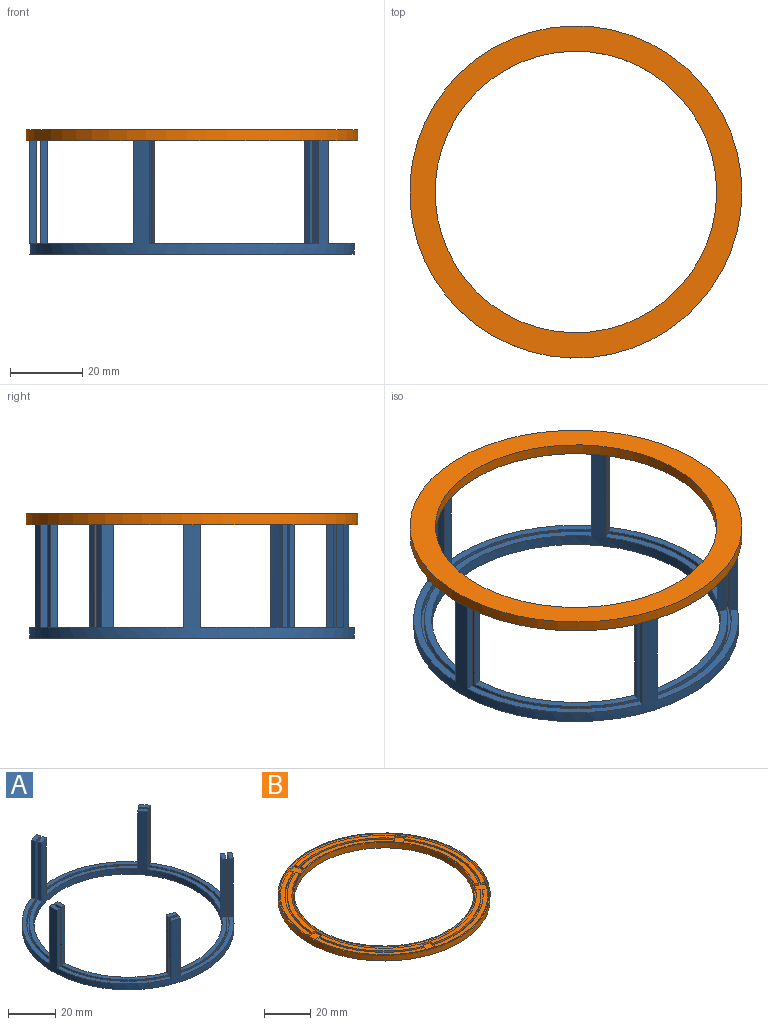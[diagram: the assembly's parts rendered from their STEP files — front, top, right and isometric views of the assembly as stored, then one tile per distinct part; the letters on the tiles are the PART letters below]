
ASSEMBLY  parts=2 mates=1
PART A: 46 faces, bbox 90x90x33 mm
  f0: plane 37.12x27.61mm, normal (0,0,1), area 94.5mm2, adj f10,f14,f16,f44
  f1: plane 39.76x29.53mm, normal (0,0,1), area 101.4mm2, adj f11,f15,f19,f41
  f2: plane 43.51x16.83mm, normal (0,0,1), area 94.5mm2, adj f10,f14,f38,f43
  f3: plane 46.62x17.94mm, normal (0,0,1), area 101.4mm2, adj f11,f15,f35,f40
  f4: plane 49.02x8.94mm, normal (0,0,1), area 101.4mm2, adj f11,f15,f32,f34
  f5: plane 45.75x8.45mm, normal (0,0,1), area 94.5mm2, adj f10,f14,f29,f37
  f6: plane 46.62x17.94mm, normal (0,0,1), area 101.4mm2, adj f11,f15,f26,f31
  f7: plane 43.51x16.83mm, normal (0,0,1), area 94.5mm2, adj f10,f14,f23,f28
  f8: plane 39.76x29.53mm, normal (0,0,1), area 101.4mm2, adj f11,f15,f20,f25
  f9: plane 37.12x27.61mm, normal (0,0,1), area 94.5mm2, adj f10,f14,f17,f22
  f10: cylinder r=40mm len=80mm, axis (0,0,-1), area 1382.3mm2, adj f0,f2,f5,f7,f9,f13,f16,f17
  f11: cylinder r=45mm len=90mm, axis (0,0,-1), area 1555.1mm2, adj f1,f3,f4,f6,f8,f13,f19,f20
  f12: plane 86x86mm, normal (0,0,1), area 267mm2, adj f14,f15
  f13: plane 90x90mm, normal (0,0,-1), area 1335.2mm2, adj f10,f11
  f14: cylinder r=42mm len=84mm, axis (0,0,-1), area 1187.5mm2, adj f0,f2,f5,f7,f9,f12,f16,f17
  f15: cylinder r=43mm len=86mm, axis (0,0,-1), area 1215.8mm2, adj f1,f3,f4,f6,f8,f12,f19,f20
  f16: plane 30x2mm, normal (0.05,1,0), area 60mm2, adj f0,f10,f14,f18
  f17: plane 30x2mm, normal (0.05,-1,0), area 60mm2, adj f9,f10,f14,f18
  f18: plane 4.4x2.06mm, normal (0,0,1), area 8.6mm2, adj f10,f14,f16,f17
  f19: plane 30x2mm, normal (0.05,1,0), area 60mm2, adj f1,f11,f15,f21
  f20: plane 30x2mm, normal (0.05,-1,0), area 60mm2, adj f8,f11,f15,f21
  f21: plane 4.71x2.06mm, normal (0,0,1), area 9.2mm2, adj f11,f15,f19,f20
  f22: plane 30x1.87mm, normal (-0.93,0.36,0), area 60mm2, adj f9,f10,f14,f24
  f23: plane 30x1.93mm, normal (0.97,-0.26,0), area 60mm2, adj f7,f10,f14,f24
  f24: plane 4.7x3.23mm, normal (0,0,1), area 8.6mm2, adj f10,f14,f22,f23
  f25: plane 30x1.87mm, normal (-0.93,0.36,0), area 60mm2, adj f8,f11,f15,f27
  f26: plane 30x1.93mm, normal (0.97,-0.26,0), area 60mm2, adj f6,f11,f15,f27
  f27: plane 5x3.32mm, normal (0,0,1), area 9.2mm2, adj f11,f15,f25,f26
  f28: plane 30x1.55mm, normal (-0.63,-0.78,0), area 60mm2, adj f7,f10,f14,f30
  f29: plane 30x1.68mm, normal (0.54,0.84,0), area 60mm2, adj f5,f10,f14,f30
  f30: plane 4.65x4.14mm, normal (0,0,1), area 8.6mm2, adj f10,f14,f28,f29
  f31: plane 30x1.55mm, normal (-0.63,-0.78,0), area 60mm2, adj f6,f11,f15,f33
  f32: plane 30x1.68mm, normal (0.54,0.84,0), area 60mm2, adj f4,f11,f15,f33
  f33: plane 4.9x4.32mm, normal (0,0,1), area 9.2mm2, adj f11,f15,f31,f32
  f34: plane 30x1.68mm, normal (0.54,-0.84,0), area 60mm2, adj f4,f11,f15,f36
  f35: plane 30x1.55mm, normal (-0.63,0.78,0), area 60mm2, adj f3,f11,f15,f36
  f36: plane 4.9x4.32mm, normal (0,0,1), area 9.2mm2, adj f11,f15,f34,f35
  f37: plane 30x1.68mm, normal (0.54,-0.84,0), area 60mm2, adj f5,f10,f14,f39
  f38: plane 30x1.55mm, normal (-0.63,0.78,0), area 60mm2, adj f2,f10,f14,f39
  f39: plane 4.65x4.14mm, normal (0,0,1), area 8.6mm2, adj f10,f14,f37,f38
  f40: plane 30x1.93mm, normal (0.97,0.26,0), area 60mm2, adj f3,f11,f15,f42
  f41: plane 30x1.87mm, normal (-0.93,-0.36,0), area 60mm2, adj f1,f11,f15,f42
  f42: plane 5x3.32mm, normal (0,0,1), area 9.2mm2, adj f11,f15,f40,f41
  f43: plane 30x1.93mm, normal (0.97,0.26,0), area 60mm2, adj f2,f10,f14,f45
  f44: plane 30x1.87mm, normal (-0.93,-0.36,0), area 60mm2, adj f0,f10,f14,f45
  f45: plane 4.7x3.23mm, normal (0,0,1), area 8.6mm2, adj f10,f14,f43,f44
PART B: 58 faces, bbox 92x92x3 mm
  f0: plane 43.39x16.77mm, normal (0,0,1), area 94.2mm2, adj f10,f25,f50,f55
  f1: plane 45.63x8.42mm, normal (0,0,1), area 94.2mm2, adj f11,f25,f52,f56
  f2: plane 43.39x16.77mm, normal (0,0,1), area 94.2mm2, adj f13,f25,f46,f53
  f3: plane 37.02x27.54mm, normal (0,0,1), area 94.2mm2, adj f12,f25,f44,f49
  f4: plane 37.02x27.54mm, normal (0,0,1), area 94.2mm2, adj f14,f25,f43,f47
  f5: plane 48.89x8.9mm, normal (0,0,1), area 101.1mm2, adj f15,f24,f30,f40
  f6: plane 46.49x17.88mm, normal (0,0,1), area 101.1mm2, adj f16,f24,f37,f42
  f7: plane 39.66x29.45mm, normal (0,0,1), area 101.1mm2, adj f17,f24,f34,f39
  f8: plane 39.66x29.45mm, normal (0,0,1), area 101.1mm2, adj f18,f24,f31,f36
  f9: plane 46.49x17.88mm, normal (0,0,1), area 101.1mm2, adj f24,f26,f28,f33
  f10: cylinder r=42mm len=43.39mm, axis (0,0,1), area 48.2mm2, adj f0,f27,f50,f55
  f11: cylinder r=42mm len=45.63mm, axis (0,0,1), area 48.2mm2, adj f1,f27,f52,f56
  f12: cylinder r=42mm len=36.91mm, axis (0,0,1), area 48.2mm2, adj f3,f27,f44,f49
  f13: cylinder r=42mm len=43.39mm, axis (0,0,1), area 48.2mm2, adj f2,f27,f46,f53
  f14: cylinder r=42mm len=36.91mm, axis (0,0,1), area 48.2mm2, adj f4,f27,f43,f47
  f15: cylinder r=43mm len=46.71mm, axis (0,0,1), area 49.4mm2, adj f5,f27,f30,f40
  f16: cylinder r=43mm len=44.43mm, axis (0,0,1), area 49.4mm2, adj f6,f27,f37,f42
  f17: cylinder r=43mm len=37.79mm, axis (0,0,1), area 49.4mm2, adj f7,f27,f34,f39
  f18: cylinder r=43mm len=37.79mm, axis (0,0,1), area 49.4mm2, adj f8,f27,f31,f36
  f19: cylinder r=39mm len=78mm, axis (0,0,-1), area 735.1mm2, adj f21,f23
  f20: cylinder r=46mm len=92mm, axis (0,0,-1), area 867.1mm2, adj f21,f22
  f21: plane 92x92mm, normal (0,0,-1), area 1869.2mm2, adj f19,f20
  f22: plane 92x92mm, normal (0,0,1), area 143.7mm2, adj f20,f24
  f23: plane 79x79mm, normal (0,0,1), area 123.3mm2, adj f19,f25
  f24: cone r=45mm half-angle=45deg, axis (0,0,1), area 201mm2, adj f5,f6,f7,f8,f9,f22,f29,f32
  f25: cone r=39.5mm half-angle=45deg, axis (0,0,-1), area 176.6mm2, adj f0,f1,f2,f3,f4,f23,f45,f48
  f26: cylinder r=43mm len=44.43mm, axis (0,0,1), area 49.4mm2, adj f9,f27,f28,f33
  f27: plane 88x86.97mm, normal (0,0,1), area 359mm2, adj f10,f11,f12,f13,f14,f15,f16,f17
  f28: plane 1.55x1.26mm, normal (0.63,0.78,0), area 2mm2, adj f9,f26,f27,f29
  f29: cylinder r=45mm len=3.94mm, axis (0,0,1), area 4.9mm2, adj f24,f27,f28,f30
  f30: plane 1.68x1.09mm, normal (-0.54,-0.84,0), area 2mm2, adj f5,f15,f27,f29
  f31: plane 1.87x1mm, normal (0.93,-0.36,0), area 2mm2, adj f8,f18,f27,f32
  f32: cylinder r=45mm len=4.63mm, axis (0,0,1), area 4.9mm2, adj f24,f27,f31,f33
  f33: plane 1.93x1mm, normal (-0.97,0.26,0), area 2mm2, adj f9,f26,f27,f32
  f34: plane 2x1mm, normal (-0.05,-1,0), area 2mm2, adj f7,f17,f27,f35
  f35: cylinder r=45mm len=4.87mm, axis (0,0,1), area 4.9mm2, adj f24,f27,f34,f36
  f36: plane 2x1mm, normal (-0.05,1,0), area 2mm2, adj f8,f18,f27,f35
  f37: plane 1.93x1mm, normal (-0.97,-0.26,0), area 2mm2, adj f6,f16,f27,f38
  f38: cylinder r=45mm len=4.63mm, axis (0,0,1), area 4.9mm2, adj f24,f27,f37,f39
  f39: plane 1.87x1mm, normal (0.93,0.36,0), area 2mm2, adj f7,f17,f27,f38
  f40: plane 1.68x1.09mm, normal (-0.54,0.84,0), area 2mm2, adj f5,f15,f27,f41
  f41: cylinder r=45mm len=3.94mm, axis (0,0,1), area 4.9mm2, adj f24,f27,f40,f42
  f42: plane 1.55x1.26mm, normal (0.63,-0.78,0), area 2mm2, adj f6,f16,f27,f41
  f43: plane 2x1mm, normal (-0.05,-1,0), area 2mm2, adj f4,f14,f27,f45
  f44: plane 2x1mm, normal (-0.05,1,0), area 2mm2, adj f3,f12,f27,f45
  f45: cylinder r=40mm len=4.33mm, axis (0,0,1), area 4.3mm2, adj f25,f27,f43,f44
  f46: plane 1.93x1mm, normal (-0.97,-0.26,0), area 2mm2, adj f2,f13,f27,f48
  f47: plane 1.87x1mm, normal (0.93,0.36,0), area 2mm2, adj f4,f14,f27,f48
  f48: cylinder r=40mm len=4.11mm, axis (0,0,1), area 4.3mm2, adj f25,f27,f46,f47
  f49: plane 1.87x1mm, normal (0.93,-0.36,0), area 2mm2, adj f3,f12,f27,f51
  f50: plane 1.93x1mm, normal (-0.97,0.26,0), area 2mm2, adj f0,f10,f27,f51
  f51: cylinder r=40mm len=4.11mm, axis (0,0,1), area 4.3mm2, adj f25,f27,f49,f50
  f52: plane 1.68x1.09mm, normal (-0.54,0.84,0), area 2mm2, adj f1,f11,f27,f54
  f53: plane 1.55x1.26mm, normal (0.63,-0.78,0), area 2mm2, adj f2,f13,f27,f54
  f54: cylinder r=40mm len=3.5mm, axis (0,0,1), area 4.3mm2, adj f25,f27,f52,f53
  f55: plane 1.55x1.26mm, normal (0.63,0.78,0), area 2mm2, adj f0,f10,f27,f57
  f56: plane 1.68x1.09mm, normal (-0.54,-0.84,0), area 2mm2, adj f1,f11,f27,f57
  f57: cylinder r=40mm len=3.5mm, axis (0,0,1), area 4.3mm2, adj f25,f27,f55,f56
PLACE A t=(-32.98,-29.8,-17.46)mm
PLACE B rot(axis=(1,0,0),180deg) t=(-32.98,-29.8,17.04)mm
MATE revolute B.f19 <-> A.f10  axis (0,0,1) through (-32.98,-29.8,15.54)mm
